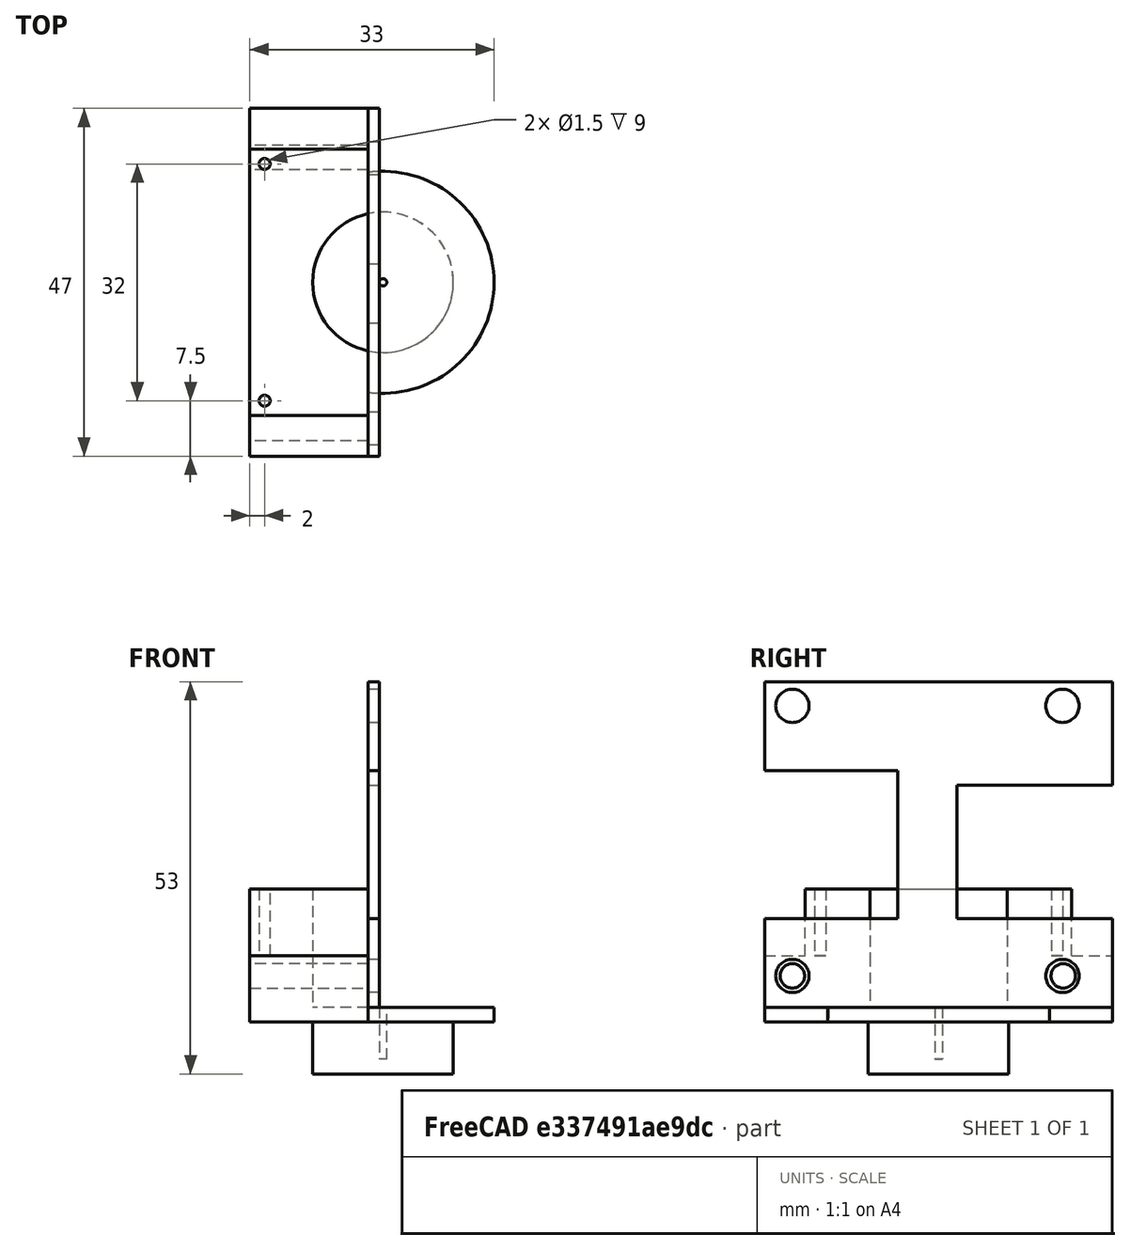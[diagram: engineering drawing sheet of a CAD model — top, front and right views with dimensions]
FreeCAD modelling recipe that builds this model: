
FCSTD DOCUMENT  (FreeCAD 0.20R29603 (Git))
Label: Quak_XL30_PCBHolder01
License: All rights reserved
LicenseURL: http://en.wikipedia.org/wiki/All_rights_reserved
objects: TechDraw::DrawViewDimension×30, Part::Cylinder×12, TechDraw::DrawProjGroupItem×8, Part::Cut×6, Part::Box×5, Part::Compound×5, App::Link×1, Part::MultiFuse×1, Part::Feature×1, TechDraw::DrawSVGTemplate×1, TechDraw::DrawProjGroup×1, TechDraw::DrawPage×1
note: 30 computed .brp shape members not serialized (recipe doc carries the construction recipe); baked Part::Feature solids carry a one-line shape summary decoded from their .brp
EXTERNAL_REF file=Quak_XL30_PCBHolder01_ModulationCoil.FCStd obj=Fusion038_solid

FEATURE [Part::Cylinder] Cylinder  label="Zylinder"
  Angle = 360
  AttacherType = Attacher::AttachEngine3D
  FirstAngle = 0
  Height = 7
  Radius = 9.5
  SecondAngle = 0
FEATURE [Part::Cylinder] Cylinder001  label="Zylinder001"
  Angle = 360
  AttacherType = Attacher::AttachEngine3D
  FirstAngle = 0
  Height = 2
  Placement = pos=(0,0,7) rot=(0,0,1;0rad)
  Radius = 15
  SecondAngle = 0
FEATURE [App::Link] Link  label="Modulation coil"
  LinkPlacement = pos=(0,0,42) rot=(0,1,0;-1.5708rad)
  LinkedObject = -> <external Quak_XL30_PCBHolder01_ModulationCoil.FCStd>#Fusion038_solid
  Placement = pos=(0,0,42) rot=(0,1,0;-1.5708rad)
FEATURE [Part::Box] Box  label="Würfel"
  AttacherType = Attacher::AttachEngine3D
  Height = 1.5
  Length = 44
  Placement = pos=(0,0,0) rot=(0,0,1;1.5708rad)
  Width = 47
FEATURE [Part::Cylinder] Cylinder002  label="Zylinder002"
  Angle = 360
  AttacherType = Attacher::AttachEngine3D
  FirstAngle = 0
  Height = 10
  Placement = pos=(-6.75,4.25,-1) rot=(0,0,1;0rad)
  Radius = 2.25
  SecondAngle = 0
FEATURE [Part::Cylinder] Cylinder003  label="Zylinder003"
  Angle = 360
  AttacherType = Attacher::AttachEngine3D
  FirstAngle = 0
  Height = 10
  Placement = pos=(-43.25,4.25,-1) rot=(0,0,1;0rad)
  Radius = 2.25
  SecondAngle = 0
FEATURE [Part::Cylinder] Cylinder004  label="Zylinder004"
  Angle = 360
  AttacherType = Attacher::AttachEngine3D
  FirstAngle = 0
  Height = 10
  Placement = pos=(-6.75,40.75,-1) rot=(0,0,1;0rad)
  Radius = 2.25
  SecondAngle = 0
FEATURE [Part::Cylinder] Cylinder005  label="Zylinder005"
  Angle = 360
  AttacherType = Attacher::AttachEngine3D
  FirstAngle = 0
  Height = 10
  Placement = pos=(-43.25,40.75,-1) rot=(0,0,1;0rad)
  Radius = 2.25
  SecondAngle = 0
FEATURE [Part::Compound] Compound
  Links = -> [Cylinder005,Cylinder002,Cylinder003,Cylinder004]
FEATURE [Part::Cut] Cut
  Base = -> Box
  Tool = -> Compound
FEATURE [Part::Box] Box001  label="Würfel001"
  AttacherType = Attacher::AttachEngine3D
  Height = 10
  Length = 18
  Placement = pos=(-47,12,-1) rot=(0,0,1;0rad)
  Width = 20
FEATURE [Part::Box] Box002  label="Würfel002"
  AttacherType = Attacher::AttachEngine3D
  Height = 10
  Length = 21
  Placement = pos=(-21,12,-1) rot=(0,0,1;0rad)
  Width = 18
FEATURE [Part::Compound] Compound001
  Links = -> [Box001,Box002]
FEATURE [Part::Cut] Cut001
  Base = -> Cut
  Placement = pos=(23.5,2,9) rot=(1,0,0;1.5708rad)
  Tool = -> Compound001
FEATURE [Part::Compound] Compound002  label="PCB"
  Links = -> [Cut001]
  Placement = pos=(0,0,0) rot=(0,0,1;1.5708rad)
FEATURE [Part::Box] Box003  label="Würfel003"
  AttacherType = Attacher::AttachEngine3D
  Height = 16
  Length = 16
  Placement = pos=(-18,-18,9) rot=(0,0,1;0rad)
  Width = 36
FEATURE [Part::Box] Box004  label="Würfel004"
  AttacherType = Attacher::AttachEngine3D
  Height = 9
  Length = 16
  Placement = pos=(-18,-23.5,7) rot=(0,0,1;0rad)
  Width = 47
FEATURE [Part::MultiFuse] Fusion
  Shapes = -> [Cylinder,Cylinder001,Box003,Box004]
FEATURE [Part::Cylinder] Cylinder006  label="Zylinder006"
  Angle = 360
  AttacherType = Attacher::AttachEngine3D
  FirstAngle = 0
  Height = 100
  Placement = pos=(-40,16.85,13.25) rot=(0,1,0;1.5708rad)
  Radius = 1.65
  SecondAngle = 0
FEATURE [Part::Cylinder] Cylinder007  label="Zylinder007"
  Angle = 360
  AttacherType = Attacher::AttachEngine3D
  FirstAngle = 0
  Height = 100
  Placement = pos=(-40,-19.75,13.25) rot=(0,1,0;1.5708rad)
  Radius = 1.65
  SecondAngle = 0
FEATURE [Part::Compound] Compound003
  Links = -> [Cylinder006,Cylinder007]
FEATURE [Part::Cut] Cut002
  Base = -> Fusion
  Tool = -> Compound003
FEATURE [Part::Cylinder] Cylinder008  label="Zylinder008"
  Angle = 360
  AttacherType = Attacher::AttachEngine3D
  FirstAngle = 0
  Height = 10
  Placement = pos=(-16,16,16) rot=(0,0,1;0rad)
  Radius = 0.75
  SecondAngle = 0
FEATURE [Part::Cylinder] Cylinder009  label="Zylinder009"
  Angle = 360
  AttacherType = Attacher::AttachEngine3D
  FirstAngle = 0
  Height = 10
  Placement = pos=(-16,-16,16) rot=(0,0,1;0rad)
  Radius = 0.75
  SecondAngle = 0
FEATURE [Part::Compound] Compound004  label="M1 holes for modulation coil"
  Links = -> [Cylinder008,Cylinder009]
FEATURE [Part::Cut] Cut003
  Base = -> Cut002
  Tool = -> Compound004
FEATURE [Part::Cylinder] Cylinder010  label="Zylinder010"
  Angle = 360
  AttacherType = Attacher::AttachEngine3D
  FirstAngle = 0
  Height = 50
  Placement = pos=(0,0,9) rot=(0,0,1;0rad)
  Radius = 9.5
  SecondAngle = 0
FEATURE [Part::Cut] Cut004
  Base = -> Cut003
  Tool = -> Cylinder010
FEATURE [Part::Cylinder] Cylinder011  label="Zylinder011"
  Angle = 360
  AttacherType = Attacher::AttachEngine3D
  FirstAngle = 0
  Height = 10
  Placement = pos=(0,0,2) rot=(0,0,1;0rad)
  Radius = 0.5
  SecondAngle = 0
FEATURE [Part::Cut] Cut005
  Base = -> Cut004
  Tool = -> Cylinder011
FEATURE [Part::Feature] Cut005_solid  label="Cut005 (Solid)"
  shape: bbox 33 x 47 x 25 mm, 35 faces (baked)
FEATURE [TechDraw::DrawSVGTemplate] Template
  EditableTexts = AuthorName=Thomas Spielauer; CreationDate=2023-08-04; FC-Scale=mm; FC-Title=SEM QUAK Holder; Subtitle=Simple holder for QUAK PCB (RT) and modulation coil
  Height = 297
  Orientation = 1
  Width = 420
FEATURE [TechDraw::DrawProjGroupItem] ProjItem  label="Front"
  CoarseView = false
  Direction = (1,0,0)
  Focus = 100
  HardHidden = false
  IsoCount = 0
  IsoHidden = false
  IsoVisible = false
  LockPosition = true
  Perspective = false
  Rotation = 0
  RotationVector = (0,1,0)
  ScaleType = 2
  SeamHidden = false
  SeamVisible = true
  SmoothHidden = false
  SmoothVisible = true
  Source = -> [Cut005_solid]
  Type = 0
  X = 0
  XDirection = (0,1,0)
  Y = 0
FEATURE [TechDraw::DrawProjGroupItem] ProjItem001  label="Right"
  CoarseView = false
  Direction = (1e-16,1,0)
  Focus = 100
  HardHidden = false
  IsoCount = 0
  IsoHidden = false
  IsoVisible = false
  LockPosition = false
  Perspective = false
  Rotation = 0
  RotationVector = (1,0,0)
  ScaleType = 2
  SeamHidden = false
  SeamVisible = true
  SmoothHidden = false
  SmoothVisible = true
  Source = -> [Cut005_solid]
  Type = 2
  X = -129.43
  XDirection = (-1,1e-16,0)
  Y = 0
FEATURE [TechDraw::DrawProjGroupItem] ProjItem002  label="Left"
  CoarseView = false
  Direction = (1e-16,-1,0)
  Focus = 100
  HardHidden = false
  IsoCount = 0
  IsoHidden = false
  IsoVisible = false
  LockPosition = false
  Perspective = false
  Rotation = 0
  RotationVector = (1,0,0)
  ScaleType = 2
  SeamHidden = false
  SeamVisible = true
  SmoothHidden = false
  SmoothVisible = true
  Source = -> [Cut005_solid]
  Type = 1
  X = 156.196
  XDirection = (1,1e-16,0)
  Y = 0
FEATURE [TechDraw::DrawProjGroupItem] ProjItem003  label="Bottom"
  CoarseView = false
  Direction = (0,0,-1)
  Focus = 100
  HardHidden = false
  IsoCount = 0
  IsoHidden = false
  IsoVisible = false
  LockPosition = false
  Perspective = false
  Rotation = 0
  RotationVector = (1,0,0)
  ScaleType = 2
  SeamHidden = false
  SeamVisible = true
  SmoothHidden = false
  SmoothVisible = true
  Source = -> [Cut005_solid]
  Type = 5
  X = 0
  XDirection = (0,1,0)
  Y = 95.9723
FEATURE [TechDraw::DrawProjGroupItem] ProjItem004  label="Top"
  CoarseView = false
  Direction = (0,0,1)
  Focus = 100
  HardHidden = false
  IsoCount = 0
  IsoHidden = false
  IsoVisible = false
  LockPosition = false
  Perspective = false
  Rotation = 0
  RotationVector = (1,0,0)
  ScaleType = 2
  SeamHidden = false
  SeamVisible = true
  SmoothHidden = false
  SmoothVisible = true
  Source = -> [Cut005_solid]
  Type = 4
  X = 0
  XDirection = (0,1,0)
  Y = -103.179
FEATURE [TechDraw::DrawProjGroupItem] ProjItem005  label="FrontBottomLeft"
  CoarseView = false
  Direction = (0.57735,-0.57735,-0.57735)
  Focus = 100
  HardHidden = false
  IsoCount = 0
  IsoHidden = false
  IsoVisible = false
  LockPosition = false
  Perspective = false
  Rotation = 0
  RotationVector = (1,0,0)
  ScaleType = 2
  SeamHidden = false
  SeamVisible = true
  SmoothHidden = false
  SmoothVisible = true
  Source = -> [Cut005_solid]
  Type = 8
  X = 155.681
  XDirection = (0.707107,0.707107,0)
  Y = 95.4575
FEATURE [TechDraw::DrawProjGroupItem] ProjItem007  label="FrontBottomRight"
  CoarseView = false
  Direction = (0.57735,0.57735,-0.57735)
  Focus = 100
  HardHidden = false
  IsoCount = 0
  IsoHidden = false
  IsoVisible = false
  LockPosition = false
  Perspective = false
  Rotation = 0
  RotationVector = (1,0,0)
  ScaleType = 2
  SeamHidden = false
  SeamVisible = true
  SmoothHidden = false
  SmoothVisible = true
  Source = -> [Cut005_solid]
  Type = 9
  X = -127.371
  XDirection = (-0.707107,0.707107,0)
  Y = 95.9723
FEATURE [TechDraw::DrawProjGroupItem] ProjItem008  label="FrontTopRight"
  CoarseView = false
  Direction = (0.57735,0.57735,0.57735)
  Focus = 100
  HardHidden = false
  IsoCount = 0
  IsoHidden = false
  IsoVisible = false
  LockPosition = false
  Perspective = false
  Rotation = 0
  RotationVector = (1,0,0)
  ScaleType = 2
  SeamHidden = false
  SeamVisible = true
  SmoothHidden = false
  SmoothVisible = true
  Source = -> [Cut005_solid]
  Type = 7
  X = -130.459
  XDirection = (-0.707107,0.707107,0)
  Y = -102.149
FEATURE [TechDraw::DrawProjGroup] ProjGroup
  Anchor = -> ProjItem
  AutoDistribute = false
  LockPosition = false
  ProjectionType = 0
  Rotation = 0
  ScaleType = 0
  Source = -> [Cut005_solid]
  Views = -> [ProjItem,ProjItem001,ProjItem002,ProjItem003,ProjItem004,ProjItem005,ProjItem007,ProjItem008]
  X = 185.808
  Y = 155.706
  spacingX = 15
  spacingY = 15
FEATURE [TechDraw::DrawViewDimension] Dimension
  AngleOverride = false
  Arbitrary = false
  ArbitraryTolerances = false
  EqualTolerance = true
  ExtensionAngle = 0
  FormatSpec = %.2w
  FormatSpecOverTolerance = %+.2w
  FormatSpecUnderTolerance = %+.2w
  Inverted = false
  LineAngle = 0
  LockPosition = false
  MeasureType = 1
  OverTolerance = 0
  References2D = -> [ProjItem003]
  Rotation = 0
  ScaleType = 0
  TheoreticalExact = false
  Type = 0
  UnderTolerance = 0
  X = -1.88836
  Y = -39.5028
FEATURE [TechDraw::DrawViewDimension] Dimension001
  AngleOverride = false
  Arbitrary = false
  ArbitraryTolerances = false
  EqualTolerance = true
  ExtensionAngle = 0
  FormatSpec = %.2w
  FormatSpecOverTolerance = %+.2w
  FormatSpecUnderTolerance = %+.2w
  Inverted = false
  LineAngle = 0
  LockPosition = false
  MeasureType = 1
  OverTolerance = 0
  References2D = -> [ProjItem003]
  Rotation = 0
  ScaleType = 0
  TheoreticalExact = false
  Type = 0
  UnderTolerance = 0
  X = 46.3491
  Y = -4.87694
FEATURE [TechDraw::DrawViewDimension] Dimension002
  AngleOverride = false
  Arbitrary = false
  ArbitraryTolerances = false
  EqualTolerance = true
  ExtensionAngle = 0
  FormatSpec = ⌀%.2w
  FormatSpecOverTolerance = %+.2w
  FormatSpecUnderTolerance = %+.2w
  Inverted = false
  LineAngle = 0
  LockPosition = false
  MeasureType = 1
  OverTolerance = 0
  References2D = -> [ProjItem003]
  Rotation = 0
  ScaleType = 0
  TheoreticalExact = false
  Type = 5
  UnderTolerance = 0
  X = 34.1792
  Y = 17.0403
FEATURE [TechDraw::DrawViewDimension] Dimension003
  AngleOverride = false
  Arbitrary = false
  ArbitraryTolerances = false
  EqualTolerance = true
  ExtensionAngle = 0
  FormatSpec = ⌀%.2w
  FormatSpecOverTolerance = %+.2w
  FormatSpecUnderTolerance = %+.2w
  Inverted = false
  LineAngle = 0
  LockPosition = false
  MeasureType = 1
  OverTolerance = 0
  References2D = -> [ProjItem003]
  Rotation = 0
  ScaleType = 0
  TheoreticalExact = false
  Type = 5
  UnderTolerance = 0
  X = 29.0807
  Y = 24.2161
FEATURE [TechDraw::DrawViewDimension] Dimension004
  AngleOverride = false
  Arbitrary = false
  ArbitraryTolerances = false
  EqualTolerance = true
  ExtensionAngle = 0
  FormatSpec = %.2w
  FormatSpecOverTolerance = %+.2w
  FormatSpecUnderTolerance = %+.2w
  Inverted = false
  LineAngle = 0
  LockPosition = false
  MeasureType = 1
  OverTolerance = 0
  References2D = -> [ProjItem004]
  Rotation = 0
  ScaleType = 0
  TheoreticalExact = false
  Type = 0
  UnderTolerance = 0
  X = 0.314726
  Y = 36.1625
FEATURE [TechDraw::DrawViewDimension] Dimension005
  AngleOverride = false
  Arbitrary = false
  ArbitraryTolerances = false
  EqualTolerance = true
  ExtensionAngle = 0
  FormatSpec = %.2w
  FormatSpecOverTolerance = %+.2w
  FormatSpecUnderTolerance = %+.2w
  Inverted = false
  LineAngle = 0
  LockPosition = false
  MeasureType = 1
  OverTolerance = 0
  References2D = -> [ProjItem004]
  Rotation = 0
  ScaleType = 0
  TheoreticalExact = false
  Type = 0
  UnderTolerance = 0
  X = -0.157363
  Y = 45.919
FEATURE [TechDraw::DrawViewDimension] Dimension006
  AngleOverride = false
  Arbitrary = false
  ArbitraryTolerances = false
  EqualTolerance = true
  ExtensionAngle = 0
  FormatSpec = %.2w
  FormatSpecOverTolerance = %+.2w
  FormatSpecUnderTolerance = %+.2w
  Inverted = false
  LineAngle = 0
  LockPosition = false
  MeasureType = 1
  OverTolerance = 0
  References2D = -> [ProjItem004]
  Rotation = 0
  ScaleType = 0
  TheoreticalExact = false
  Type = 0
  UnderTolerance = 0
  X = -32.9418
  Y = 11.01
FEATURE [TechDraw::DrawViewDimension] Dimension007
  AngleOverride = false
  Arbitrary = false
  ArbitraryTolerances = false
  EqualTolerance = true
  ExtensionAngle = 0
  FormatSpec = ⌀%.2w
  FormatSpecOverTolerance = %+.2w
  FormatSpecUnderTolerance = %+.2w
  Inverted = false
  LineAngle = 0
  LockPosition = false
  MeasureType = 1
  OverTolerance = 0
  References2D = -> [ProjItem004]
  Rotation = 0
  ScaleType = 0
  TheoreticalExact = false
  Type = 5
  UnderTolerance = 0
  X = -30.8716
  Y = -13.0724
FEATURE [TechDraw::DrawViewDimension] Dimension008
  AngleOverride = false
  Arbitrary = false
  ArbitraryTolerances = false
  EqualTolerance = true
  ExtensionAngle = 0
  FormatSpec = ⌀%.2w
  FormatSpecOverTolerance = %+.2w
  FormatSpecUnderTolerance = %+.2w
  Inverted = false
  LineAngle = 0
  LockPosition = false
  MeasureType = 1
  OverTolerance = 0
  References2D = -> [ProjItem004]
  Rotation = 0
  ScaleType = 0
  TheoreticalExact = false
  Type = 5
  UnderTolerance = 0
  X = 19.4882
  Y = -10.4314
FEATURE [TechDraw::DrawViewDimension] Dimension009
  AngleOverride = false
  Arbitrary = false
  ArbitraryTolerances = false
  EqualTolerance = true
  ExtensionAngle = 0
  FormatSpec = ⌀%.2w (2x M2)
  FormatSpecOverTolerance = %+.2w
  FormatSpecUnderTolerance = %+.2w
  Inverted = false
  LineAngle = 0
  LockPosition = false
  MeasureType = 1
  OverTolerance = 0
  References2D = -> [ProjItem004]
  Rotation = 0
  ScaleType = 0
  TheoreticalExact = false
  Type = 5
  UnderTolerance = 0
  X = 48.7611
  Y = 32.8552
FEATURE [TechDraw::DrawViewDimension] Dimension010
  AngleOverride = false
  Arbitrary = false
  ArbitraryTolerances = false
  EqualTolerance = true
  ExtensionAngle = 0
  FormatSpec = %.2w
  FormatSpecOverTolerance = %+.2w
  FormatSpecUnderTolerance = %+.2w
  Inverted = false
  LineAngle = 0
  LockPosition = false
  MeasureType = 1
  OverTolerance = 0
  References2D = -> [ProjItem]
  Rotation = 0
  ScaleType = 0
  TheoreticalExact = false
  Type = 0
  UnderTolerance = 0
  X = 38.7957
  Y = -9.83501
FEATURE [TechDraw::DrawViewDimension] Dimension011
  AngleOverride = false
  Arbitrary = false
  ArbitraryTolerances = false
  EqualTolerance = true
  ExtensionAngle = 0
  FormatSpec = %.2w
  FormatSpecOverTolerance = %+.2w
  FormatSpecUnderTolerance = %+.2w
  Inverted = false
  LineAngle = 0
  LockPosition = false
  MeasureType = 1
  OverTolerance = 0
  References2D = -> [ProjItem]
  Rotation = 0
  ScaleType = 0
  TheoreticalExact = false
  Type = 0
  UnderTolerance = 0
  X = 54.8229
  Y = 17.2932
FEATURE [TechDraw::DrawViewDimension] Dimension012
  AngleOverride = false
  Arbitrary = false
  ArbitraryTolerances = false
  EqualTolerance = true
  ExtensionAngle = 0
  FormatSpec = %.2w
  FormatSpecOverTolerance = %+.2w
  FormatSpecUnderTolerance = %+.2w
  Inverted = false
  LineAngle = 0
  LockPosition = false
  MeasureType = 1
  OverTolerance = 0
  References2D = -> [ProjItem004]
  Rotation = 0
  ScaleType = 0
  TheoreticalExact = false
  Type = 0
  UnderTolerance = 0
  X = 31.0974
  Y = 9.67742
FEATURE [TechDraw::DrawViewDimension] Dimension013
  AngleOverride = false
  Arbitrary = false
  ArbitraryTolerances = false
  EqualTolerance = true
  ExtensionAngle = 0
  FormatSpec = %.2w
  FormatSpecOverTolerance = %+.2w
  FormatSpecUnderTolerance = %+.2w
  Inverted = false
  LineAngle = 0
  LockPosition = false
  MeasureType = 1
  OverTolerance = 0
  References2D = -> [ProjItem004]
  Rotation = 0
  ScaleType = 0
  TheoreticalExact = false
  Type = 0
  UnderTolerance = 0
  X = -12.1669
  Y = -29.8343
FEATURE [TechDraw::DrawViewDimension] Dimension014
  AngleOverride = false
  Arbitrary = false
  ArbitraryTolerances = false
  EqualTolerance = true
  ExtensionAngle = 0
  FormatSpec = %.2w
  FormatSpecOverTolerance = %+.2w
  FormatSpecUnderTolerance = %+.2w
  Inverted = false
  LineAngle = 0
  LockPosition = false
  MeasureType = 1
  OverTolerance = 0
  References2D = -> [ProjItem004]
  Rotation = 0
  ScaleType = 0
  TheoreticalExact = false
  Type = 0
  UnderTolerance = 0
  X = -46.9698
  Y = 24.4743
FEATURE [TechDraw::DrawViewDimension] Dimension015
  AngleOverride = false
  Arbitrary = false
  ArbitraryTolerances = false
  EqualTolerance = true
  ExtensionAngle = 0
  FormatSpec = %.2w
  FormatSpecOverTolerance = %+.2w
  FormatSpecUnderTolerance = %+.2w
  Inverted = false
  LineAngle = 0
  LockPosition = false
  MeasureType = 1
  OverTolerance = 0
  References2D = -> [ProjItem004]
  Rotation = 0
  ScaleType = 0
  TheoreticalExact = false
  Type = 0
  UnderTolerance = 0
  X = -60.7749
  Y = 10.4888
FEATURE [TechDraw::DrawViewDimension] Dimension016
  AngleOverride = false
  Arbitrary = false
  ArbitraryTolerances = false
  EqualTolerance = true
  ExtensionAngle = 0
  FormatSpec = %.2w
  FormatSpecOverTolerance = %+.2w
  FormatSpecUnderTolerance = %+.2w
  Inverted = false
  LineAngle = 0
  LockPosition = false
  MeasureType = 1
  OverTolerance = 0
  References2D = -> [ProjItem002]
  Rotation = 0
  ScaleType = 0
  TheoreticalExact = false
  Type = 0
  UnderTolerance = 0
  X = 24.4675
  Y = 2.47559
FEATURE [TechDraw::DrawViewDimension] Dimension017
  AngleOverride = false
  Arbitrary = false
  ArbitraryTolerances = false
  EqualTolerance = true
  ExtensionAngle = 0
  FormatSpec = %.2w
  FormatSpecOverTolerance = %+.2w
  FormatSpecUnderTolerance = %+.2w
  Inverted = false
  LineAngle = 0
  LockPosition = false
  MeasureType = 1
  OverTolerance = 0
  References2D = -> [ProjItem002]
  Rotation = 0
  ScaleType = 0
  TheoreticalExact = false
  Type = 0
  UnderTolerance = 0
  X = -41.4258
  Y = 9.25399
FEATURE [TechDraw::DrawViewDimension] Dimension018
  AngleOverride = false
  Arbitrary = false
  ArbitraryTolerances = false
  EqualTolerance = true
  ExtensionAngle = 0
  FormatSpec = %.2w
  FormatSpecOverTolerance = %+.2w
  FormatSpecUnderTolerance = %+.2w
  Inverted = false
  LineAngle = 0
  LockPosition = false
  MeasureType = 1
  OverTolerance = 0
  References2D = -> [ProjItem002]
  Rotation = 0
  ScaleType = 0
  TheoreticalExact = false
  Type = 0
  UnderTolerance = 0
  X = -33.0112
  Y = 19.7839
FEATURE [TechDraw::DrawViewDimension] Dimension019
  AngleOverride = false
  Arbitrary = false
  ArbitraryTolerances = false
  EqualTolerance = true
  ExtensionAngle = 0
  FormatSpec = %.2w
  FormatSpecOverTolerance = %+.2w
  FormatSpecUnderTolerance = %+.2w
  Inverted = false
  LineAngle = 0
  LockPosition = false
  MeasureType = 1
  OverTolerance = 0
  References2D = -> [ProjItem002]
  Rotation = 0
  ScaleType = 0
  TheoreticalExact = false
  Type = 0
  UnderTolerance = 0
  X = -21.2328
  Y = -16.9957
FEATURE [TechDraw::DrawViewDimension] Dimension020
  AngleOverride = false
  Arbitrary = false
  ArbitraryTolerances = false
  EqualTolerance = true
  ExtensionAngle = 0
  FormatSpec = %.2w
  FormatSpecOverTolerance = %+.2w
  FormatSpecUnderTolerance = %+.2w
  Inverted = false
  LineAngle = 0
  LockPosition = false
  MeasureType = 1
  OverTolerance = 0
  References2D = -> [ProjItem002]
  Rotation = 0
  ScaleType = 0
  TheoreticalExact = false
  Type = 0
  UnderTolerance = 0
  X = -9.95245
  Y = 25.8794
FEATURE [TechDraw::DrawViewDimension] Dimension021
  AngleOverride = false
  Arbitrary = false
  ArbitraryTolerances = false
  EqualTolerance = true
  ExtensionAngle = 0
  FormatSpec = %.2w
  FormatSpecOverTolerance = %+.2w
  FormatSpecUnderTolerance = %+.2w
  Inverted = false
  LineAngle = 0
  LockPosition = false
  MeasureType = 1
  OverTolerance = 0
  References2D = -> [ProjItem002]
  Rotation = 0
  ScaleType = 0
  TheoreticalExact = false
  Type = 0
  UnderTolerance = 0
  X = 1.3464
  Y = -29.8289
FEATURE [TechDraw::DrawViewDimension] Dimension022
  AngleOverride = false
  Arbitrary = false
  ArbitraryTolerances = false
  EqualTolerance = true
  ExtensionAngle = 0
  FormatSpec = %.2w
  FormatSpecOverTolerance = %+.2w
  FormatSpecUnderTolerance = %+.2w
  Inverted = false
  LineAngle = 0
  LockPosition = false
  MeasureType = 1
  OverTolerance = 0
  References2D = -> [ProjItem002]
  Rotation = 0
  ScaleType = 0
  TheoreticalExact = false
  Type = 0
  UnderTolerance = 0
  X = 0.178884
  Y = -43.2269
FEATURE [TechDraw::DrawViewDimension] Dimension023
  AngleOverride = false
  Arbitrary = false
  ArbitraryTolerances = false
  EqualTolerance = true
  ExtensionAngle = 0
  FormatSpec = ⌀%.2w (M4 x2)
  FormatSpecOverTolerance = %+.2w
  FormatSpecUnderTolerance = %+.2w
  Inverted = false
  LineAngle = 0
  LockPosition = false
  MeasureType = 1
  OverTolerance = 0
  References2D = -> [ProjItem]
  Rotation = 0
  ScaleType = 0
  TheoreticalExact = false
  Type = 5
  UnderTolerance = 0
  X = 40.4021
  Y = 32.228
FEATURE [TechDraw::DrawViewDimension] Dimension024
  AngleOverride = false
  Arbitrary = false
  ArbitraryTolerances = false
  EqualTolerance = true
  ExtensionAngle = 0
  FormatSpec = %.2w
  FormatSpecOverTolerance = %+.2w
  FormatSpecUnderTolerance = %+.2w
  Inverted = false
  LineAngle = 0
  LockPosition = false
  MeasureType = 1
  OverTolerance = 0
  References2D = -> [ProjItem]
  Rotation = 0
  ScaleType = 0
  TheoreticalExact = false
  Type = 0
  UnderTolerance = 0
  X = -41.4553
  Y = 9.81885
FEATURE [TechDraw::DrawViewDimension] Dimension025
  AngleOverride = false
  Arbitrary = false
  ArbitraryTolerances = false
  EqualTolerance = true
  ExtensionAngle = 0
  FormatSpec = %.2w
  FormatSpecOverTolerance = %+.2w
  FormatSpecUnderTolerance = %+.2w
  Inverted = false
  LineAngle = 0
  LockPosition = false
  MeasureType = 1
  OverTolerance = 0
  References2D = -> [ProjItem]
  Rotation = 0
  ScaleType = 0
  TheoreticalExact = false
  Type = 0
  UnderTolerance = 0
  X = -10.7237
  Y = 28.8307
FEATURE [TechDraw::DrawViewDimension] Dimension026
  AngleOverride = false
  Arbitrary = false
  ArbitraryTolerances = false
  EqualTolerance = true
  ExtensionAngle = 0
  FormatSpec = %.2w
  FormatSpecOverTolerance = %+.2w
  FormatSpecUnderTolerance = %+.2w
  Inverted = false
  LineAngle = 0
  LockPosition = false
  MeasureType = 1
  OverTolerance = 0
  References2D = -> [ProjItem]
  Rotation = 0
  ScaleType = 0
  TheoreticalExact = false
  Type = 0
  UnderTolerance = 0
  X = -6.17089
  Y = -28.4171
FEATURE [TechDraw::DrawViewDimension] Dimension027
  AngleOverride = false
  Arbitrary = false
  ArbitraryTolerances = false
  EqualTolerance = true
  ExtensionAngle = 0
  FormatSpec = %.2w
  FormatSpecOverTolerance = %+.2w
  FormatSpecUnderTolerance = %+.2w
  Inverted = false
  LineAngle = 0
  LockPosition = false
  MeasureType = 1
  OverTolerance = 0
  References2D = -> [ProjItem]
  Rotation = 0
  ScaleType = 0
  TheoreticalExact = false
  Type = 0
  UnderTolerance = 0
  X = 7.66966
  Y = 28.6768
FEATURE [TechDraw::DrawViewDimension] Dimension028
  AngleOverride = false
  Arbitrary = false
  ArbitraryTolerances = false
  EqualTolerance = true
  ExtensionAngle = 0
  FormatSpec = %.2w
  FormatSpecOverTolerance = %+.2w
  FormatSpecUnderTolerance = %+.2w
  Inverted = false
  LineAngle = 0
  LockPosition = false
  MeasureType = 1
  OverTolerance = 0
  References2D = -> [ProjItem003]
  Rotation = 0
  ScaleType = 0
  TheoreticalExact = false
  Type = 0
  UnderTolerance = 0
  X = -43.7082
  Y = -3.17405
FEATURE [TechDraw::DrawViewDimension] Dimension029
  AngleOverride = false
  Arbitrary = false
  ArbitraryTolerances = false
  EqualTolerance = true
  ExtensionAngle = 0
  FormatSpec = %.2w
  FormatSpecOverTolerance = %+.2w
  FormatSpecUnderTolerance = %+.2w
  Inverted = false
  LineAngle = 0
  LockPosition = false
  MeasureType = 1
  OverTolerance = 0
  References2D = -> [ProjItem003]
  Rotation = 0
  ScaleType = 0
  TheoreticalExact = false
  Type = 0
  UnderTolerance = 0
  X = -10.8331
  Y = 29.9959
FEATURE [TechDraw::DrawPage] Page
  KeepUpdated = true
  NextBalloonIndex = 1
  ProjectionType = 0
  Template = -> Template
  Views = -> [ProjGroup,Dimension,Dimension001,Dimension002,Dimension003,Dimension004,Dimension005,Dimension006,Dimension007,Dimension008,Dimension009,Dimension010,Dimension011,Dimension012,Dimension013,Dimension014,Dimension015,Dimension016,Dimension017,Dimension018,Dimension019,Dimension020,Dimension021,Dimension022,Dimension023,Dimension024,Dimension025,Dimension026,Dimension027,Dimension028,Dimension029]
